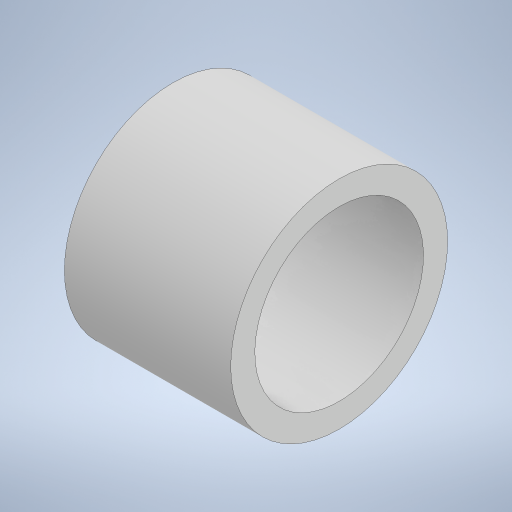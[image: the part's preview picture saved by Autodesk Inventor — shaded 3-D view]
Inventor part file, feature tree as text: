
AUTODESK INVENTOR PART (.ipt)
format: ipt  version: 2023 (Build 270158000, 158)  size: 210,944 bytes
history: native  units: mm
features: other x1, extrude x1, sketch x1
ambient origin geometry x8: Origin, YZ Plane, XZ Plane, XY Plane, X Axis, Y Axis, Z Axis, Center Point
bodies: Body1 (feature_tree)
feature tree (3):
  other  "Bryła1"
  extrude  "Wyciągnięcie proste1"  Depth=14.0mm
  sketch  "Szkic1"
